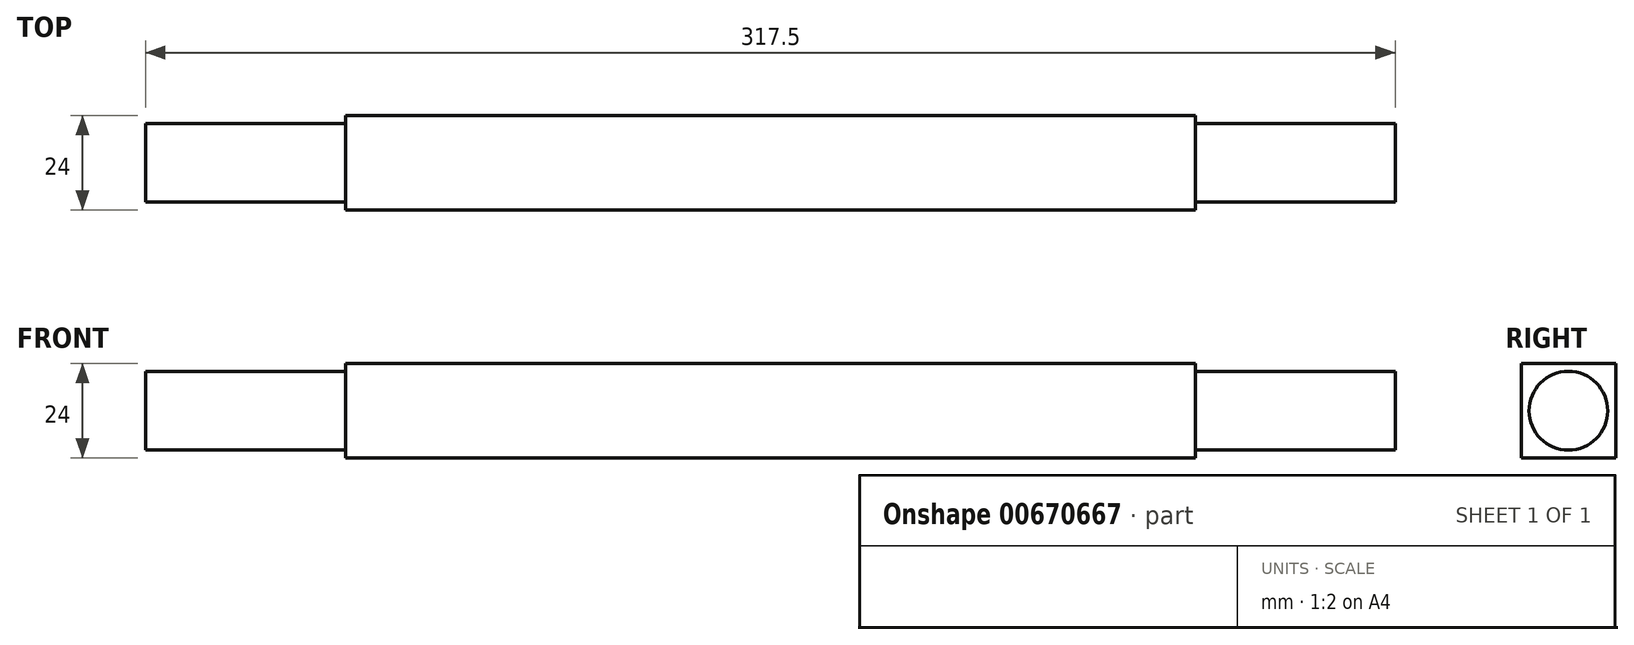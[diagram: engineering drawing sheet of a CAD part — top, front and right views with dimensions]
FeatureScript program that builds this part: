
annotation { "Feature Type Name" : "Feature", "Feature Type Description" : "" }
export const myFeature = defineFeature(function(context is Context, id is Id, definition is map)
    precondition{}
    {
        {
            var Q0;
            Q0=qCreatedBy(makeId("Right.planeOp"),FACE);
            var sketch = newSketch(context, id + "F0", { "sketchPlane" : qUnion([Q0])});
            skCircle(sketch, "E0", {"center": v(0, 0) * mm, "radius": 10 * mm});
            skLineSegment(sketch, "E1.bottom", {"start": v(-10, -10) * mm, "end": v(10, -10) * mm});
            skLineSegment(sketch, "E1.top", {"start": v(-10, 10) * mm, "end": v(10, 10) * mm});
            skLineSegment(sketch, "E1.left", {"start": v(-10, -10) * mm, "end": v(-10, 10) * mm});
            skLineSegment(sketch, "E1.right", {"start": v(10, -10) * mm, "end": v(10, 10) * mm});
            skSolve(sketch);
        }
        {
            var Q0;
            {var subQ0=sQuery(id+"F0.wireOp",EDGE,"E1.top");var subQ1=sQuery(id+"F0.wireOp",EDGE,"E0");var subQ2=makeQuery(id+"F0.imprint","INTERSECT",VERTEX,{"derivedFrom":[subQ1,subQ0]});Q0=makeQuery(id+"F0.imprint","IMPRINT",FACE,{"disambiguationData":[TD([[makeQuery(id+"F0.imprint","IMPRINT",EDGE,{"disambiguationData":[TD([[subQ2,-1.0]])],"derivedFrom":subQ1}),-1.0]])]});}
            var Q1;
            {var subQ0=sQuery(id+"F0.wireOp",EDGE,"E1.top");var subQ1=sQuery(id+"F0.wireOp",EDGE,"E0");var subQ2=makeQuery(id+"F0.imprint","INTERSECT",VERTEX,{"derivedFrom":[subQ1,subQ0]});Q1=makeQuery(id+"F0.imprint","IMPRINT",FACE,{"disambiguationData":[TD([[makeQuery(id+"F0.imprint","IMPRINT",EDGE,{"disambiguationData":[TD([[subQ2,1.0]])],"derivedFrom":subQ1}),-1.0]])]});}
            var Q2;
            {var subQ0=sQuery(id+"F0.wireOp",EDGE,"E1.right");var subQ1=sQuery(id+"F0.wireOp",EDGE,"E0");var subQ2=makeQuery(id+"F0.imprint","INTERSECT",VERTEX,{"derivedFrom":[subQ1,subQ0]});Q2=makeQuery(id+"F0.imprint","IMPRINT",FACE,{"disambiguationData":[TD([[makeQuery(id+"F0.imprint","IMPRINT",EDGE,{"disambiguationData":[TD([[subQ2,1.0]])],"derivedFrom":subQ1}),-1.0]])]});}
            var Q3;
            {var subQ0=sQuery(id+"F0.wireOp",EDGE,"E1.left");var subQ1=sQuery(id+"F0.wireOp",EDGE,"E0");var subQ2=makeQuery(id+"F0.imprint","INTERSECT",VERTEX,{"derivedFrom":[subQ1,subQ0]});Q3=makeQuery(id+"F0.imprint","IMPRINT",FACE,{"disambiguationData":[TD([[makeQuery(id+"F0.imprint","IMPRINT",EDGE,{"disambiguationData":[TD([[subQ2,-1.0]])],"derivedFrom":subQ1}),-1.0]])]});}
            extrude(context, id + "F1", {"entities" : qUnion([Q0, Q1, Q2, Q3]), "endBound" : BoundingType.SYMMETRIC, "depth" : 215.9 * mm, "offsetDistance" : 25 * mm});
        }
        {
            var Q0;
            {var subQ0=sQuery(id+"F0.wireOp",EDGE,"E0");var subQ1=makeQuery(id+"F0.imprint","INTERSECT",VERTEX,{"derivedFrom":[subQ0,sQuery(id+"F0.wireOp",EDGE,"E1.top")]});Q0=makeQuery(id+"F0.imprint","IMPRINT",FACE,{"disambiguationData":[TD([[makeQuery(id+"F0.imprint","IMPRINT",EDGE,{"disambiguationData":[TD([[subQ1,1.0]])],"derivedFrom":subQ0}),1.0]])]});}
            extrude(context, id + "F2", {"entities" : qUnion([Q0]), "endBound" : BoundingType.SYMMETRIC, "depth" : 317.5 * mm, "offsetDistance" : 25 * mm});
        }
        {
            var Q0;
            Q0=makeQuery(id+"F1.opExtrude","SWEPT_BODY",BODY,{"disambiguationData":[OSD([sQuery(id+"F0.wireOp",EDGE,"E0"),sQuery(id+"F0.wireOp",EDGE,"E1.top"),sQuery(id+"F0.wireOp",EDGE,"E1.left")])]});
            var Q1;
            Q1=makeQuery(id+"F1.opExtrude","SWEPT_BODY",BODY,{"disambiguationData":[OSD([sQuery(id+"F0.wireOp",EDGE,"E0"),sQuery(id+"F0.wireOp",EDGE,"E1.top"),sQuery(id+"F0.wireOp",EDGE,"E1.right")])]});
            var Q2;
            Q2=makeQuery(id+"F2.opExtrude","SWEPT_BODY",BODY,{"disambiguationData":[OSD([sQuery(id+"F0.wireOp",EDGE,"E0")])]});
            var Q3;
            Q3=makeQuery(id+"F1.opExtrude","SWEPT_BODY",BODY,{"disambiguationData":[OSD([sQuery(id+"F0.wireOp",EDGE,"E0"),sQuery(id+"F0.wireOp",EDGE,"E1.bottom"),sQuery(id+"F0.wireOp",EDGE,"E1.right")])]});
            var Q4;
            Q4=makeQuery(id+"F1.opExtrude","SWEPT_BODY",BODY,{"disambiguationData":[OSD([sQuery(id+"F0.wireOp",EDGE,"E0"),sQuery(id+"F0.wireOp",EDGE,"E1.bottom"),sQuery(id+"F0.wireOp",EDGE,"E1.left")])]});
            booleanBodies(context, id + "F3", {"operationType" : BooleanOperationType.UNION, "tools" : qUnion([Q0, Q1, Q2, Q3, Q4])});
        }
        {
            var Q0;
            {var subQ0=sQuery(id+"F0.wireOp",EDGE,"E1.top");Q0=makeQuery(id+"F3.opBoolean","MERGE",FACE,{"derivedFrom":[makeQuery(id+"F1.opExtrude","SWEPT_FACE",FACE,{"disambiguationData":[OSD([subQ0]),TDD([makeQuery(id+"F0.imprint","IMPRINT",EDGE,{"disambiguationData":[TD([[makeQuery(id+"F0.imprint","INTERSECT",VERTEX,{"derivedFrom":[subQ0,sQuery(id+"F0.wireOp",EDGE,"E1.left")]}),-1.0]])],"derivedFrom":subQ0})])]}),makeQuery(id+"F1.opExtrude","SWEPT_FACE",FACE,{"disambiguationData":[OSD([subQ0]),TDD([makeQuery(id+"F0.imprint","IMPRINT",EDGE,{"disambiguationData":[TD([[makeQuery(id+"F0.imprint","INTERSECT",VERTEX,{"derivedFrom":[subQ0,sQuery(id+"F0.wireOp",EDGE,"E1.right")]}),1.0]])],"derivedFrom":subQ0})])]})]});}
            extrude(context, id + "F4", {"entities" : qUnion([Q0]), "operationType" : NewBodyOperationType.ADD, "depth" : 2 * mm, "offsetDistance" : 25 * mm});
        }
        {
            var Q0;
            {var subQ0=sQuery(id+"F0.wireOp",EDGE,"E1.left");var subQ1=sQuery(id+"F0.wireOp",EDGE,"E1.top");Q0=makeQuery(id+"F4.boolean.opBoolean","MERGE",FACE,{"derivedFrom":[makeQuery(id+"F3.opBoolean","MERGE",FACE,{"derivedFrom":[makeQuery(id+"F1.opExtrude","SWEPT_FACE",FACE,{"disambiguationData":[OSD([subQ0]),TDD([makeQuery(id+"F0.imprint","IMPRINT",EDGE,{"disambiguationData":[TD([[makeQuery(id+"F0.imprint","INTERSECT",VERTEX,{"derivedFrom":[sQuery(id+"F0.wireOp",EDGE,"E1.bottom"),subQ0]}),-1.0]])],"derivedFrom":subQ0})])]}),makeQuery(id+"F1.opExtrude","SWEPT_FACE",FACE,{"disambiguationData":[OSD([subQ0]),TDD([makeQuery(id+"F0.imprint","IMPRINT",EDGE,{"disambiguationData":[TD([[makeQuery(id+"F0.imprint","INTERSECT",VERTEX,{"derivedFrom":[subQ1,subQ0]}),1.0]])],"derivedFrom":subQ0})])]})]}),makeQuery(id+"F4.opExtrude","SWEPT_FACE",FACE,{"disambiguationData":[OSD([subQ1,subQ0])]})]});}
            extrude(context, id + "F5", {"entities" : qUnion([Q0]), "operationType" : NewBodyOperationType.ADD, "depth" : 2 * mm, "offsetDistance" : 25 * mm});
        }
        {
            var Q0;
            {var subQ0=sQuery(id+"F0.wireOp",EDGE,"E1.right");var subQ1=sQuery(id+"F0.wireOp",EDGE,"E1.top");Q0=makeQuery(id+"F4.boolean.opBoolean","MERGE",FACE,{"derivedFrom":[makeQuery(id+"F3.opBoolean","MERGE",FACE,{"derivedFrom":[makeQuery(id+"F1.opExtrude","SWEPT_FACE",FACE,{"disambiguationData":[OSD([subQ0]),TDD([makeQuery(id+"F0.imprint","IMPRINT",EDGE,{"disambiguationData":[TD([[makeQuery(id+"F0.imprint","INTERSECT",VERTEX,{"derivedFrom":[sQuery(id+"F0.wireOp",EDGE,"E1.bottom"),subQ0]}),-1.0]])],"derivedFrom":subQ0})])]}),makeQuery(id+"F1.opExtrude","SWEPT_FACE",FACE,{"disambiguationData":[OSD([subQ0]),TDD([makeQuery(id+"F0.imprint","IMPRINT",EDGE,{"disambiguationData":[TD([[makeQuery(id+"F0.imprint","INTERSECT",VERTEX,{"derivedFrom":[subQ1,subQ0]}),1.0]])],"derivedFrom":subQ0})])]})]}),makeQuery(id+"F4.opExtrude","SWEPT_FACE",FACE,{"disambiguationData":[OSD([subQ1,subQ0])]})]});}
            extrude(context, id + "F6", {"entities" : qUnion([Q0]), "operationType" : NewBodyOperationType.ADD, "depth" : 2 * mm, "offsetDistance" : 25 * mm});
        }
        {
            var Q0;
            {var subQ0=sQuery(id+"F0.wireOp",EDGE,"E1.right");var subQ1=sQuery(id+"F0.wireOp",EDGE,"E1.bottom");var subQ2=sQuery(id+"F0.wireOp",EDGE,"E1.left");Q0=makeQuery(id+"F6.boolean.opBoolean","MERGE",FACE,{"derivedFrom":[makeQuery(id+"F5.boolean.opBoolean","MERGE",FACE,{"derivedFrom":[makeQuery(id+"F3.opBoolean","MERGE",FACE,{"derivedFrom":[makeQuery(id+"F1.opExtrude","SWEPT_FACE",FACE,{"disambiguationData":[OSD([subQ1]),TDD([makeQuery(id+"F0.imprint","IMPRINT",EDGE,{"disambiguationData":[TD([[makeQuery(id+"F0.imprint","INTERSECT",VERTEX,{"derivedFrom":[subQ1,subQ2]}),-1.0]])],"derivedFrom":subQ1})])]}),makeQuery(id+"F1.opExtrude","SWEPT_FACE",FACE,{"disambiguationData":[OSD([subQ1]),TDD([makeQuery(id+"F0.imprint","IMPRINT",EDGE,{"disambiguationData":[TD([[makeQuery(id+"F0.imprint","INTERSECT",VERTEX,{"derivedFrom":[subQ1,subQ0]}),1.0]])],"derivedFrom":subQ1})])]})]}),makeQuery(id+"F5.opExtrude","SWEPT_FACE",FACE,{"disambiguationData":[OSD([subQ1,subQ2])]})]}),makeQuery(id+"F6.opExtrude","SWEPT_FACE",FACE,{"disambiguationData":[OSD([subQ1,subQ0])]})]});}
            extrude(context, id + "F7", {"entities" : qUnion([Q0]), "operationType" : NewBodyOperationType.ADD, "depth" : 2 * mm, "offsetDistance" : 25 * mm});
        }
    });
